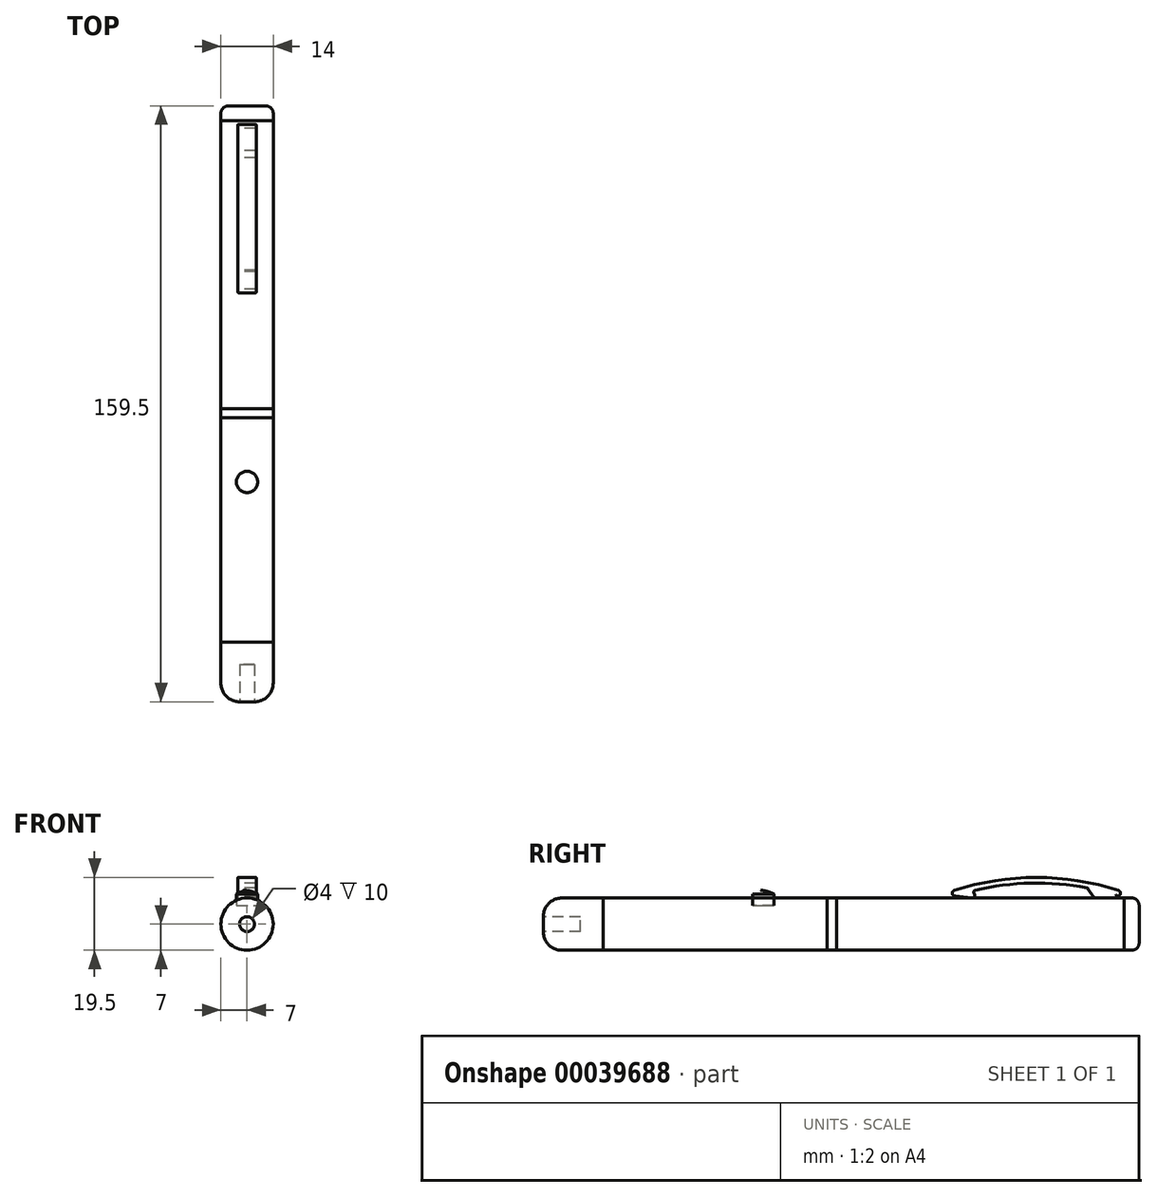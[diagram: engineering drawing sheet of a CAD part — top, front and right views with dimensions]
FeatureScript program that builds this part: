
annotation { "Feature Type Name" : "Feature", "Feature Type Description" : "" }
export const myFeature = defineFeature(function(context is Context, id is Id, definition is map)
    precondition{}
    {
        {
            var Q0;
            Q0=qCreatedBy(makeId("Front.planeOp"),FACE);
            var sketch = newSketch(context, id + "F0", { "sketchPlane" : qUnion([Q0])});
            skCircle(sketch, "E0", {"center": v(0, 0) * mm, "radius": 7 * mm});
            skSolve(sketch);
        }
        {
            var Q0;
            Q0=makeQuery(id+"F0.imprint","IMPRINT",FACE,{"disambiguationData":[TD([[makeQuery(id+"F0.imprint","IMPRINT",EDGE,{"derivedFrom":sQuery(id+"F0.wireOp",EDGE,"E0")}),1.0]])]});
            extrude(context, id + "F1", {"entities" : qUnion([Q0]), "depth" : 4 * mm});
        }
        {
            var Q0;
            Q0=makeQuery(id+"F1.opExtrude","CAP_EDGE",EDGE,{"disambiguationData":[OSD([sQuery(id+"F0.wireOp",EDGE,"E0")])],"isStart":true});
            fillet(context, id + "F2", {"entities" : qUnion([Q0]), "radius" : 2 * mm, "tangentPropagation" : true, "allowEdgeOverflow" : false});
        }
        {
            var Q0;
            Q0=makeQuery(id+"F1.opExtrude","CAP_FACE",FACE,{"disambiguationData":[OSD([sQuery(id+"F0.wireOp",EDGE,"E0")])],"isStart":false});
            extrude(context, id + "F3", {"entities" : qUnion([Q0]), "depth" : 77 * mm});
        }
        {
            var Q0;
            Q0=makeQuery(id+"F3.opExtrude","CAP_FACE",FACE,{"disambiguationData":[OSD([sQuery(id+"F0.wireOp",EDGE,"E0")])],"isStart":false});
            extrude(context, id + "F4", {"entities" : qUnion([Q0]), "depth" : 2.5 * mm});
        }
        {
            var Q0;
            Q0=makeQuery(id+"F4.opExtrude","CAP_FACE",FACE,{"disambiguationData":[OSD([sQuery(id+"F0.wireOp",EDGE,"E0")])],"isStart":false});
            extrude(context, id + "F5", {"entities" : qUnion([Q0]), "depth" : 60 * mm});
        }
        {
            var Q0;
            Q0=makeQuery(id+"F5.opExtrude","CAP_FACE",FACE,{"disambiguationData":[OSD([sQuery(id+"F0.wireOp",EDGE,"E0")])],"isStart":false});
            extrude(context, id + "F6", {"entities" : qUnion([Q0]), "depth" : 16 * mm});
        }
        {
            var Q0;
            Q0=makeQuery(id+"F6.opExtrude","CAP_EDGE",EDGE,{"disambiguationData":[OSD([sQuery(id+"F0.wireOp",EDGE,"E0")])],"isStart":false});
            fillet(context, id + "F7", {"entities" : qUnion([Q0]), "radius" : 5 * mm, "tangentPropagation" : true, "allowEdgeOverflow" : false});
        }
        {
            var Q0;
            Q0=makeQuery(id+"F6.opExtrude","CAP_FACE",FACE,{"disambiguationData":[OSD([sQuery(id+"F0.wireOp",EDGE,"E0")])],"isStart":false});
            extrude(context, id + "F8", {"entities" : qUnion([Q0]), "operationType" : NewBodyOperationType.REMOVE, "oppositeDirection" : true, "depth" : 10 * mm});
        }
        {
            var Q0;
            Q0=qCreatedBy(makeId("Right.planeOp"),FACE);
            var sketch = newSketch(context, id + "F9", { "sketchPlane" : qUnion([Q0])});
            skPoint(sketch, "E1", {"position": v(-5.5, 9) * mm});
            skPoint(sketch, "E2", {"position": v(-49.5, 9) * mm});
            skPoint(sketch, "E3", {"position": v(-27.5, 12.5) * mm});
            skArc(sketch, "E4", {"start": v(-5.5, 9) * mm, "mid": v(-27.5, 12.5) * mm, "end": v(-49.5, 9) * mm});
            skArc(sketch, "E5.0", {"start": v(-13.9, 9.65) * mm, "mid": v(-28.94, 10.99) * mm, "end": v(-43.92, 9.03) * mm});
            skArc(sketch, "E6", {"start": v(-49.5, 9) * mm, "mid": v(-49.98, 8.05) * mm, "end": v(-49.03, 7.57) * mm});
            skArc(sketch, "E7", {"start": v(-5.97, 7.57) * mm, "mid": v(-5.02, 8.05) * mm, "end": v(-5.5, 9) * mm});
            skArc(sketch, "E8", {"start": v(-44.87, 7) * mm, "mid": v(-44.11, 7.38) * mm, "end": v(-44.19, 8.23) * mm});
            skLineSegment(sketch, "E9", {"start": v(-49.03, 7.57) * mm, "end": v(-44.87, 7) * mm});
            skArc(sketch, "E10", {"start": v(-43.92, 9.03) * mm, "mid": v(-44.28, 8.7) * mm, "end": v(-44.19, 8.23) * mm});
            skLineSegment(sketch, "E11", {"start": v(-5.97, 7.57) * mm, "end": v(-5.97, 7) * mm});
            skLineSegment(sketch, "E12", {"start": v(-5.97, 7) * mm, "end": v(-11.97, 7) * mm});
            skLineSegment(sketch, "E13", {"start": v(-11.97, 7) * mm, "end": v(-13.9, 9.65) * mm});
            skSolve(sketch);
        }
        {
            var Q0;
            Q0=makeQuery(id+"F9.imprint","IMPRINT",FACE,{"disambiguationData":[TD([[makeQuery(id+"F9.imprint","IMPRINT",EDGE,{"derivedFrom":sQuery(id+"F9.wireOp",EDGE,"E4")}),1.0]])]});
            extrude(context, id + "F10", {"entities" : qUnion([Q0]), "depth" : 2.5 * mm, "hasSecondDirection" : true, "secondDirectionOppositeDirection" : true, "secondDirectionDepth" : 2.5 * mm});
        }
        {
            var Q0;
            Q0=makeQuery(id+"F10.opExtrude","CAP_FACE",FACE,{"disambiguationData":[OSD([sQuery(id+"F9.wireOp",EDGE,"E4"),sQuery(id+"F9.wireOp",EDGE,"E5.0"),sQuery(id+"F9.wireOp",EDGE,"E6"),sQuery(id+"F9.wireOp",EDGE,"E7"),sQuery(id+"F9.wireOp",EDGE,"E8"),sQuery(id+"F9.wireOp",EDGE,"E9"),sQuery(id+"F9.wireOp",EDGE,"E10"),sQuery(id+"F9.wireOp",EDGE,"E11"),sQuery(id+"F9.wireOp",EDGE,"E12"),sQuery(id+"F9.wireOp",EDGE,"E13")])],"isStart":false});
            var Q1;
            Q1=makeQuery(id+"F10.opExtrude","CAP_FACE",FACE,{"disambiguationData":[OSD([sQuery(id+"F9.wireOp",EDGE,"E4"),sQuery(id+"F9.wireOp",EDGE,"E5.0"),sQuery(id+"F9.wireOp",EDGE,"E6"),sQuery(id+"F9.wireOp",EDGE,"E7"),sQuery(id+"F9.wireOp",EDGE,"E8"),sQuery(id+"F9.wireOp",EDGE,"E9"),sQuery(id+"F9.wireOp",EDGE,"E10"),sQuery(id+"F9.wireOp",EDGE,"E11"),sQuery(id+"F9.wireOp",EDGE,"E12"),sQuery(id+"F9.wireOp",EDGE,"E13")])],"isStart":true});
            fillet(context, id + "F11", {"entities" : qUnion([Q0, Q1]), "radius" : 0.2 * mm, "tangentPropagation" : true, "allowEdgeOverflow" : false});
        }
        {
            var Q0;
            Q0=qCreatedBy(makeId("Right.planeOp"),FACE);
            var sketch = newSketch(context, id + "F12", { "sketchPlane" : qUnion([Q0])});
            skLineSegment(sketch, "E14.top", {"start": v(-103.5, 5) * mm, "end": v(-100.65, 5) * mm});
            skLineSegment(sketch, "E14.left", {"start": v(-103.5, 8.04) * mm, "end": v(-103.5, 5) * mm});
            skArc(sketch, "E15", {"start": v(-100.65, 8.97) * mm, "mid": v(-102.13, 8.67) * mm, "end": v(-103.5, 8.04) * mm});
            skLineSegment(sketch, "E16", {"start": v(-100.65, 5) * mm, "end": v(-100.65, 8.97) * mm});
            skSolve(sketch);
        }
        {
            var Q0;
            Q0=makeQuery(id+"F12.imprint","IMPRINT",FACE,{"disambiguationData":[TD([[makeQuery(id+"F12.imprint","IMPRINT",EDGE,{"derivedFrom":sQuery(id+"F12.wireOp",EDGE,"E14.top")}),1.0]])]});
            var Q1;
            Q1=sQuery(id+"F12.wireOp",EDGE,"E16");
            revolve(context, id + "F13", {"entities" : qUnion([Q0]), "axis" : qUnion([Q1]), "revolveType" : RevolveType.FULL});
        }
    });
